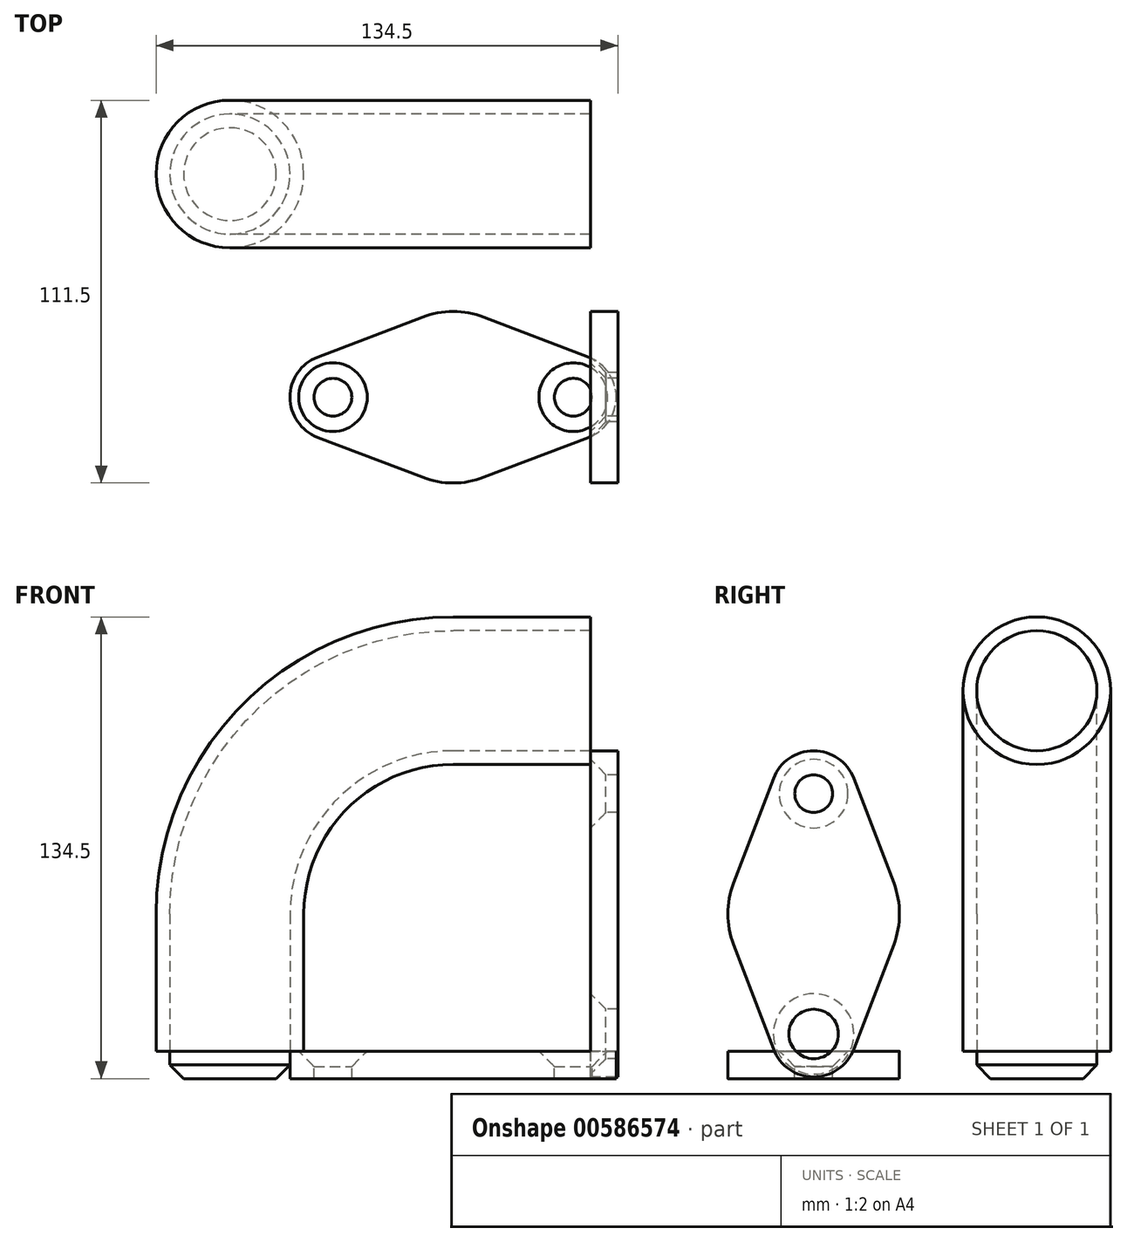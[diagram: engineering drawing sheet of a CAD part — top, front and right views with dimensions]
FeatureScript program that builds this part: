
annotation { "Feature Type Name" : "Feature", "Feature Type Description" : "" }
export const myFeature = defineFeature(function(context is Context, id is Id, definition is map)
    precondition{}
    {
        {
            var Q0;
            Q0=qCreatedBy(makeId("Front.planeOp"),FACE);
            var sketch = newSketch(context, id + "F0", { "sketchPlane" : qUnion([Q0])});
            skArc(sketch, "E0", {"start": v(-65, 0) * mm, "mid": v(-45.96, 45.96) * mm, "end": v(0, 65) * mm});
            skLineSegment(sketch, "E1", {"start": v(0, 65) * mm, "end": v(40, 65) * mm});
            skLineSegment(sketch, "E2", {"start": v(-65, -40) * mm, "end": v(-65, 0) * mm});
            skSolve(sketch);
        }
        {
            var Q0;
            Q0=qCreatedBy(makeId("Top.planeOp"),FACE);
            var sketch = newSketch(context, id + "F1", { "sketchPlane" : qUnion([Q0])});
            skCircle(sketch, "E3", {"center": v(-65, 0) * mm, "radius": 17.5 * mm});
            skCircle(sketch, "E4", {"center": v(-65, 0) * mm, "radius": 21.5 * mm});
            skSolve(sketch);
        }
        {
            var Q0;
            Q0=makeQuery(id+"F1.imprint","IMPRINT",FACE,{"disambiguationData":[TD([[makeQuery(id+"F1.imprint","IMPRINT",EDGE,{"derivedFrom":sQuery(id+"F1.wireOp",EDGE,"E3")}),-1.0]])]});
            var Q1;
            Q1=sQuery(id+"F0.wireOp",EDGE,"E0");
            var Q2;
            Q2=sQuery(id+"F0.wireOp",EDGE,"E2");
            var Q3;
            Q3=sQuery(id+"F0.wireOp",EDGE,"E1");
            sweep(context, id + "F2", {"profiles" : qUnion([Q0]), "path" : qUnion([Q1, Q2, Q3])});
        }
        {
            var Q0;
            Q0=makeQuery(id+"F2.opSweep","CAP_FACE",FACE,{"disambiguationData":[OSD([sQuery(id+"F0.wireOp",VERTEX,"E2.start"),sQuery(id+"F1.wireOp",EDGE,"E3"),sQuery(id+"F1.wireOp",EDGE,"E4")])],"isStart":true});
            var sketch = newSketch(context, id + "F3", { "sketchPlane" : qUnion([Q0])});
            skArc(sketch, "E5", {"start": v(-88.35, 8.93) * mm, "mid": v(-90, 0) * mm, "end": v(-88.35, -8.93) * mm});
            skArc(sketch, "E6", {"start": v(-53.32, 39.46) * mm, "mid": v(-65, 47.5) * mm, "end": v(-76.68, 39.46) * mm});
            skArc(sketch, "E7", {"start": v(-76.68, -39.46) * mm, "mid": v(-65, -47.5) * mm, "end": v(-53.32, -39.46) * mm});
            skLineSegment(sketch, "E8", {"start": v(-53.32, 39.46) * mm, "end": v(-41.65, 8.93) * mm});
            skLineSegment(sketch, "E9", {"start": v(-41.65, -8.93) * mm, "end": v(-53.32, -39.46) * mm});
            skLineSegment(sketch, "E10", {"start": v(-88.35, -8.93) * mm, "end": v(-76.68, -39.46) * mm});
            skLineSegment(sketch, "E11", {"start": v(-76.68, 39.46) * mm, "end": v(-88.35, 8.93) * mm});
            skArc(sketch, "E12.trimOffspring", {"start": v(-41.65, -8.93) * mm, "mid": v(-40, 0) * mm, "end": v(-41.65, 8.93) * mm});
            skCircle(sketch, "E13", {"center": v(-65, 35) * mm, "radius": 5.5 * mm});
            skCircle(sketch, "E14", {"center": v(-65, -35) * mm, "radius": 7.2 * mm});
            skCircle(sketch, "E15.0", {"center": v(-65, 0) * mm, "radius": 17.5 * mm});
            skSolve(sketch);
        }
        {
            var Q0;
            Q0=makeQuery(id+"F3.imprint","IMPRINT",FACE,{"disambiguationData":[TD([[makeQuery(id+"F3.imprint","IMPRINT",EDGE,{"derivedFrom":sQuery(id+"F3.wireOp",EDGE,"E5")}),1.0]])]});
            var Q1;
            Q1=makeQuery(id+"F3.imprint","IMPRINT",FACE,{"disambiguationData":[TD([[makeQuery(id+"F3.imprint","IMPRINT",EDGE,{"derivedFrom":sQuery(id+"F3.wireOp",EDGE,"E15.0")}),1.0]])]});
            extrude(context, id + "F4", {"entities" : qUnion([Q0, Q1]), "depth" : 8 * mm, "offsetDistance" : 25 * mm});
        }
        {
            var Q0;
            Q0=makeQuery(id+"F2.opSweep","CAP_FACE",FACE,{"disambiguationData":[OSD([sQuery(id+"F0.wireOp",VERTEX,"E1.end"),sQuery(id+"F1.wireOp",EDGE,"E3"),sQuery(id+"F1.wireOp",EDGE,"E4")])],"isStart":false});
            var sketch = newSketch(context, id + "F5", { "sketchPlane" : qUnion([Q0])});
            skArc(sketch, "E16", {"start": v(8.93, 88.35) * mm, "mid": v(0, 90) * mm, "end": v(-8.93, 88.35) * mm});
            skArc(sketch, "E17", {"start": v(39.46, 53.32) * mm, "mid": v(47.5, 65) * mm, "end": v(39.46, 76.68) * mm});
            skArc(sketch, "E18", {"start": v(-39.46, 76.68) * mm, "mid": v(-47.5, 65) * mm, "end": v(-39.46, 53.32) * mm});
            skLineSegment(sketch, "E19", {"start": v(39.46, 76.68) * mm, "end": v(8.93, 88.35) * mm});
            skLineSegment(sketch, "E20", {"start": v(39.46, 53.32) * mm, "end": v(8.93, 41.65) * mm});
            skLineSegment(sketch, "E21", {"start": v(-8.93, 88.35) * mm, "end": v(-39.46, 76.68) * mm});
            skLineSegment(sketch, "E22", {"start": v(-8.93, 41.65) * mm, "end": v(-39.46, 53.32) * mm});
            skArc(sketch, "E23.trimOffspring", {"start": v(-8.93, 41.65) * mm, "mid": v(0, 40) * mm, "end": v(8.93, 41.65) * mm});
            skCircle(sketch, "E24", {"center": v(-35, 65) * mm, "radius": 5.5 * mm});
            skCircle(sketch, "E25", {"center": v(35, 65) * mm, "radius": 5.5 * mm});
            skSolve(sketch);
        }
        {
            var Q0;
            Q0=makeQuery(id+"F5.imprint","IMPRINT",FACE,{"disambiguationData":[TD([[makeQuery(id+"F5.imprint","IMPRINT",EDGE,{"derivedFrom":sQuery(id+"F5.wireOp",EDGE,"E16")}),1.0]])]});
            var Q1;
            {var subQ0=sQuery(id+"F0.wireOp",VERTEX,"E1.end");Q1=makeQuery(id+"F5.imprint","IMPRINT",FACE,{"disambiguationData":[TD([[makeQuery(id+"F5.imprint","IMPRINT",EDGE,{"derivedFrom":makeQuery(id+"F2.opSweep","CAP_EDGE",EDGE,{"disambiguationData":[OSD([subQ0,sQuery(id+"F1.wireOp",EDGE,"E3")])],"isStart":false})}),-1.0]])]});}
            extrude(context, id + "F6", {"entities" : qUnion([Q0, Q1]), "depth" : 8 * mm, "offsetDistance" : 25 * mm});
        }
        {
            var Q0;
            Q0=makeQuery(id+"F4.opExtrude","CAP_EDGE",EDGE,{"disambiguationData":[OSD([sQuery(id+"F3.wireOp",EDGE,"E14")])],"isStart":true});
            var Q1;
            Q1=makeQuery(id+"F4.opExtrude","CAP_EDGE",EDGE,{"disambiguationData":[OSD([sQuery(id+"F3.wireOp",EDGE,"E13")])],"isStart":true});
            var Q2;
            Q2=makeQuery(id+"F6.opExtrude","CAP_EDGE",EDGE,{"disambiguationData":[OSD([sQuery(id+"F5.wireOp",EDGE,"E25")])],"isStart":true});
            var Q3;
            Q3=makeQuery(id+"F6.opExtrude","CAP_EDGE",EDGE,{"disambiguationData":[OSD([sQuery(id+"F5.wireOp",EDGE,"E24")])],"isStart":true});
            chamfer(context, id + "F7", {"entities" : qUnion([Q0, Q1, Q2, Q3]), "width" : 4.5 * mm, "tangentPropagation" : true});
        }
        {
            var Q0;
            Q0=makeQuery(id+"F4.opExtrude","CAP_EDGE",EDGE,{"disambiguationData":[OSD([sQuery(id+"F3.wireOp",EDGE,"E15.0")])],"isStart":false});
            var Q1;
            Q1=makeQuery(id+"F6.opExtrude","CAP_EDGE",EDGE,{"disambiguationData":[OSD([sQuery(id+"F0.wireOp",VERTEX,"E1.end"),sQuery(id+"F1.wireOp",EDGE,"E3")])],"isStart":false});
            chamfer(context, id + "F8", {"entities" : qUnion([Q0, Q1]), "width" : 4 * mm, "tangentPropagation" : true});
        }
    });
